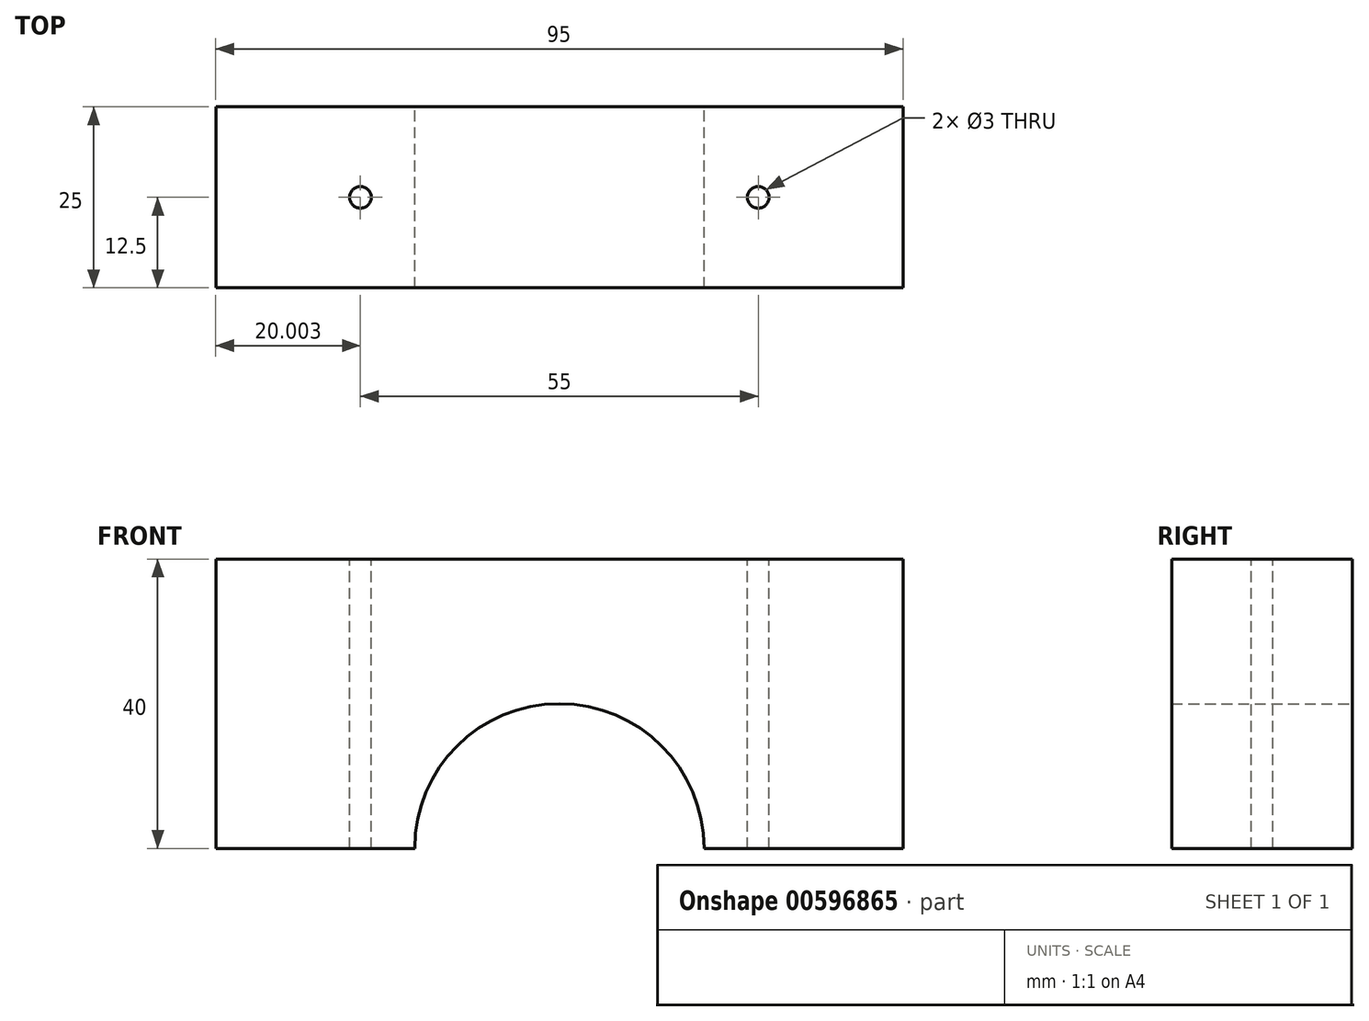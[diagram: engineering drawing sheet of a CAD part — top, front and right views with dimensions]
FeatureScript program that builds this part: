
annotation { "Feature Type Name" : "Feature", "Feature Type Description" : "" }
export const myFeature = defineFeature(function(context is Context, id is Id, definition is map)
    precondition{}
    {
        {
            var Q0;
            Q0=qCreatedBy(makeId("Front.planeOp"),FACE);
            var sketch = newSketch(context, id + "F0", { "sketchPlane" : qUnion([Q0])});
            skLineSegment(sketch, "E0.bottom", {"start": v(-49.4, 59.24) * mm, "end": v(45.6, 59.24) * mm});
            skLineSegment(sketch, "E0.top", {"start": v(-49.4, 19.24) * mm, "end": v(45.6, 19.24) * mm});
            skLineSegment(sketch, "E0.left", {"start": v(-49.4, 59.24) * mm, "end": v(-49.4, 19.24) * mm});
            skLineSegment(sketch, "E0.right", {"start": v(45.6, 59.24) * mm, "end": v(45.6, 19.24) * mm});
            skArc(sketch, "E1", {"start": v(18.1, 19.24) * mm, "mid": v(-1.9, 39.24) * mm, "end": v(-21.9, 19.24) * mm});
            skSolve(sketch);
        }
        {
            var Q0;
            Q0=makeQuery(id+"F0.imprint","IMPRINT",FACE,{"disambiguationData":[TD([[makeQuery(id+"F0.imprint","IMPRINT",EDGE,{"derivedFrom":sQuery(id+"F0.wireOp",EDGE,"E0.bottom")}),-1.0]])]});
            extrude(context, id + "F1", {"entities" : qUnion([Q0]), "depth" : 25 * mm, "offsetDistance" : 25 * mm});
        }
        {
            var Q0;
            Q0=makeQuery(id+"F1.opExtrude","SWEPT_FACE",FACE,{"disambiguationData":[OSD([sQuery(id+"F0.wireOp",EDGE,"E0.bottom")])]});
            var sketch = newSketch(context, id + "F2", { "sketchPlane" : qUnion([Q0])});
            skCircle(sketch, "E2", {"center": v(-29.4, -12.5) * mm, "radius": 1.5 * mm});
            skCircle(sketch, "E3", {"center": v(25.6, -12.5) * mm, "radius": 1.5 * mm});
            skSolve(sketch);
        }
        {
            var Q0;
            Q0 = qSketchRegion(id + "F2", true);
            extrude(context, id + "F3", {"entities" : qUnion([Q0]), "operationType" : NewBodyOperationType.REMOVE, "oppositeDirection" : true, "depth" : 40 * mm, "offsetDistance" : 25 * mm});
        }
    });
